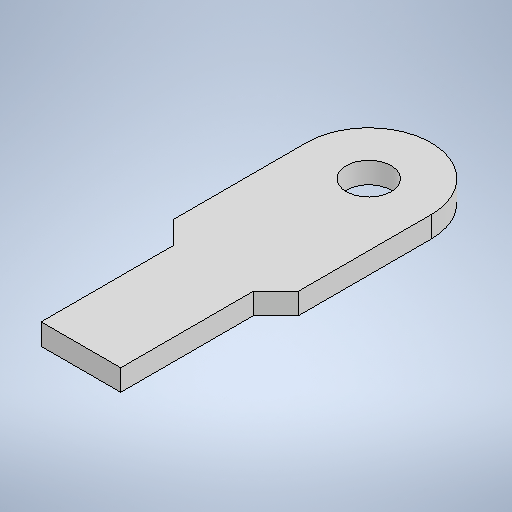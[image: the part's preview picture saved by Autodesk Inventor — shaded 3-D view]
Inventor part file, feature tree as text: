
AUTODESK INVENTOR PART (.ipt)
format: ipt  version: 2025 (Build 290162010, 162A)  size: 288,256 bytes
history: native  units: mm
features: other x2, sheet_metal_op x1, sketch x1
ambient origin geometry x8: Origin, YZ Plane, XZ Plane, XY Plane, X Axis, Y Axis, Z Axis, Center Point
bodies: Body1 (feature_tree)
feature tree (4):
  sheet_metal_op  "Face3"
  sketch  "Sketch1"  dims[d61=500.0mm d156=8.0mm d162=17.0mm d163=15.0mm d164=50.0mm d165=45.0deg d166=50.0mm d167=30.0mm]
  other  "Plate5"
  other  "Definition1"
